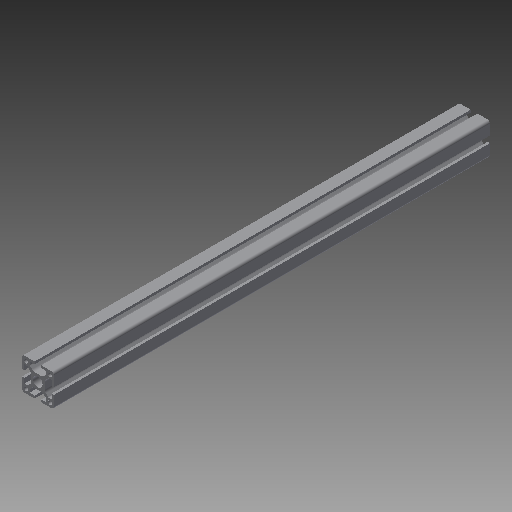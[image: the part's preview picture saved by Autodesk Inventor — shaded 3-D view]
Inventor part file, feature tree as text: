
AUTODESK INVENTOR PART (.ipt)
format: ipt  version: 2018 (Build 220112000, 112)  size: 222,208 bytes
history: native  units: mm
features: other x42, sketch x5, hole x4, extrude x1
ambient origin geometry x8: Origin, YZ Plane, XZ Plane, XY Plane, X Axis, Y Axis, Z Axis, Center Point
bodies: Solid1 (feature_tree)
feature tree (52):
  extrude  "Extrusion1"  [1 undecoded]
  hole  "Drilling 1"  [1 undecoded]
  hole  "Drilling 2"  [1 undecoded]
  hole  "Drilling 3"  [1 undecoded]
  hole  "Drilling 4"  [1 undecoded]
  other  "side_4d_XY"
  other  "side_4d_YZ"
  other  "side_4d_ZX"
  other  "side_4d_X"
  other  "side_4d_Y"
  other  "side_4d_Z"
  other  "side_4d_Center"
  other  "side_1a_XY"
  other  "side_1a_YZ"
  other  "side_1a_ZX"
  other  "side_1a_X"
  other  "side_1a_Y"
  other  "side_1a_Z"
  other  "side_1a_Center"
  other  "side_2b_XY"
  other  "side_2b_YZ"
  other  "side_2b_ZX"
  other  "side_2b_X"
  other  "side_2b_Y"
  other  "side_2b_Z"
  other  "side_2b_Center"
  other  "side_3c_XY"
  other  "side_3c_YZ"
  other  "side_3c_ZX"
  other  "side_3c_X"
  other  "side_3c_Y"
  other  "side_3c_Z"
  other  "side_3c_Center"
  other  "end_XY"
  other  "end_YZ"
  other  "end_ZX"
  other  "end_X"
  other  "end_Y"
  other  "end_Z"
  other  "end_Center"
  other  "start_XY"
  other  "start_YZ"
  other  "start_ZX"
  other  "start_X"
  other  "start_Y"
  other  "start_Z"
  other  "start_Center"
  sketch  "Skizze_1"  dims[d0=545.0mm d1=0.0mm]
  sketch  "Sketch2"  dims[d2=5.0mm d3=6.0mm d4=4.0mm d5=2.0mm d6=90.0deg d7=6000.0mm d8=0.0mm]
  sketch  "Sketch3"  dims[d9=5.0mm d10=6.0mm d11=4.0mm d12=2.0mm d13=90.0deg d14=6000.0mm d15=0.0mm]
  sketch  "Sketch4"  dims[d16=5.0mm d17=6.0mm d18=4.0mm d19=2.0mm d20=90.0deg d21=6000.0mm d22=0.0mm]
  sketch  "Sketch5"  dims[d23=5.0mm d24=6.0mm d25=4.0mm d26=2.0mm d27=90.0deg d28=6000.0mm d29=0.0mm]
note: 5 required parameter values undecoded (feature->parameter linkage not recoverable at this tier; creation-order binding heuristic only, values carry confidence <= 0.55)
